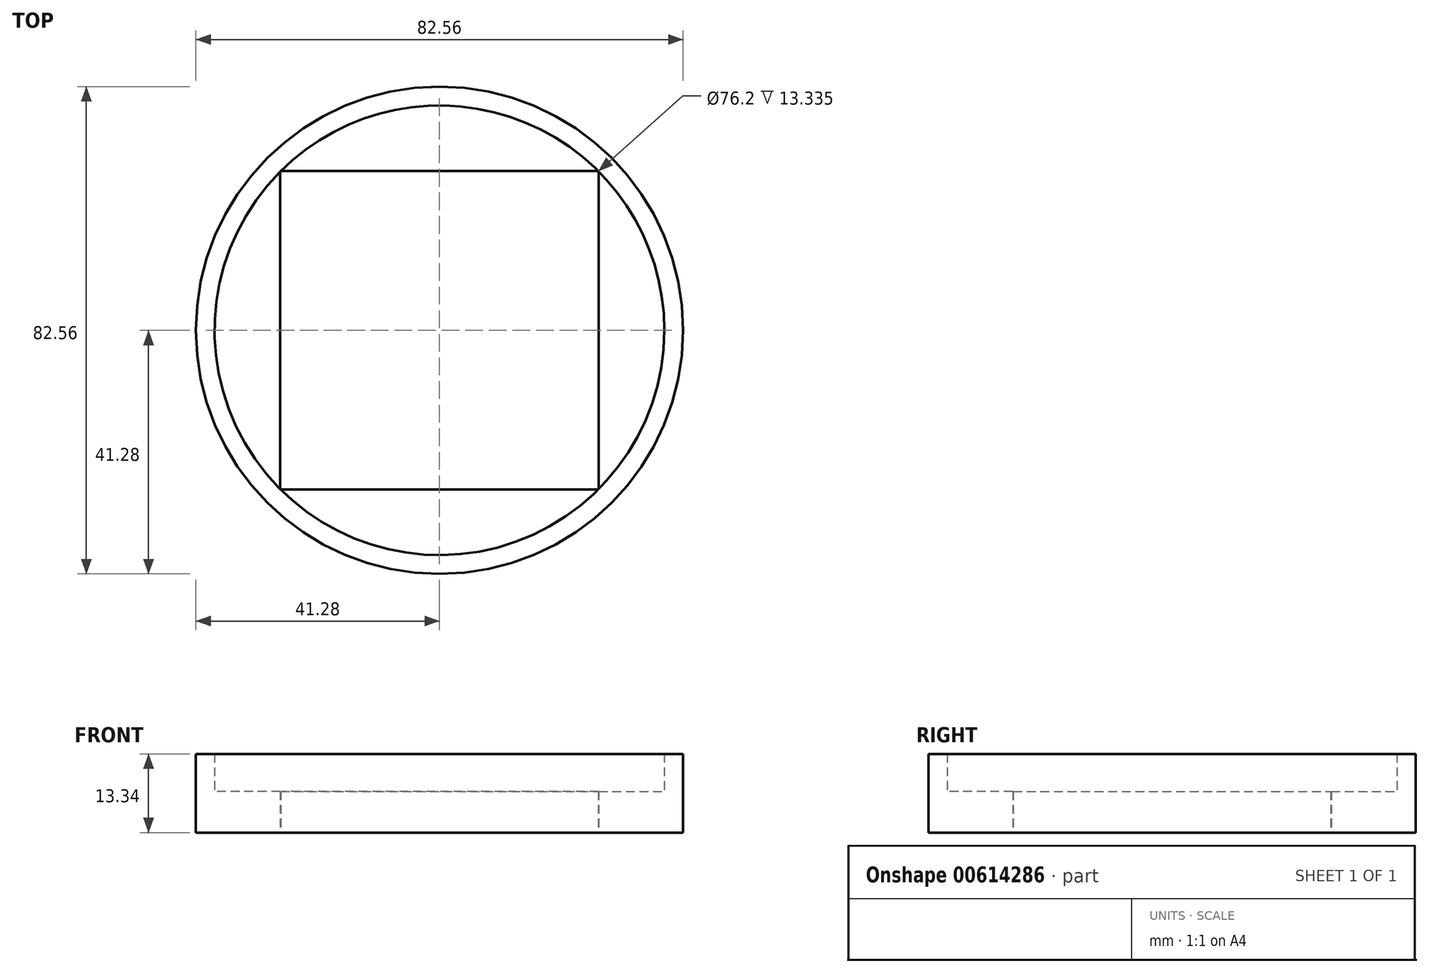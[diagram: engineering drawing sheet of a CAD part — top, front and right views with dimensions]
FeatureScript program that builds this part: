
annotation { "Feature Type Name" : "Feature", "Feature Type Description" : "" }
export const myFeature = defineFeature(function(context is Context, id is Id, definition is map)
    precondition{}
    {
        {
            var Q0;
            Q0=qCreatedBy(makeId("Top.planeOp"),FACE);
            var sketch = newSketch(context, id + "F0", { "sketchPlane" : qUnion([Q0])});
            skCircle(sketch, "E0", {"center": v(0, 0) * mm, "radius": 38.1 * mm});
            skCircle(sketch, "E1", {"center": v(0, 0) * mm, "radius": 41.28 * mm});
            skSolve(sketch);
        }
        {
            var Q0;
            Q0=makeQuery(id+"F0.imprint","IMPRINT",FACE,{"disambiguationData":[TD([[makeQuery(id+"F0.imprint","IMPRINT",EDGE,{"derivedFrom":sQuery(id+"F0.wireOp",EDGE,"E0")}),1.0]])]});
            var sketch = newSketch(context, id + "F1", { "sketchPlane" : qUnion([Q0])});
            skLineSegment(sketch, "E2.bottom", {"start": v(28.58, 28.58) * mm, "end": v(-28.57, 28.58) * mm});
            skLineSegment(sketch, "E2.top", {"start": v(28.58, -28.58) * mm, "end": v(-28.58, -28.58) * mm});
            skLineSegment(sketch, "E2.left", {"start": v(28.58, 28.58) * mm, "end": v(28.58, -28.58) * mm});
            skLineSegment(sketch, "E2.right", {"start": v(-28.57, 28.58) * mm, "end": v(-28.58, -28.58) * mm});
            skPoint(sketch, "E2.middle", {"position": v(0, 0) * mm});
            skLineSegment(sketch, "E3.bottom", {"start": v(26.99, -26.99) * mm, "end": v(-26.99, -26.99) * mm});
            skLineSegment(sketch, "E3.top", {"start": v(26.99, 26.99) * mm, "end": v(-26.99, 26.99) * mm});
            skLineSegment(sketch, "E3.left", {"start": v(26.99, -26.99) * mm, "end": v(26.99, 26.99) * mm});
            skLineSegment(sketch, "E3.right", {"start": v(-26.99, -26.99) * mm, "end": v(-26.99, 26.99) * mm});
            skSolve(sketch);
        }
        {
            var Q0;
            Q0=makeQuery(id+"F0.imprint","IMPRINT",FACE,{"disambiguationData":[TD([[makeQuery(id+"F0.imprint","IMPRINT",EDGE,{"derivedFrom":sQuery(id+"F0.wireOp",EDGE,"E0")}),-1.0]])]});
            extrude(context, id + "F2", {"entities" : qUnion([Q0]), "depth" : 13.33 * mm, "offsetDistance" : 25.4 * mm});
        }
        {
            var Q0;
            {var subQ0=sQuery(id+"F1.wireOp",EDGE,"E2.right");var subQ1=makeQuery(id+"F0.imprint","IMPRINT",EDGE,{"derivedFrom":sQuery(id+"F0.wireOp",EDGE,"E0")});var subQ2=makeQuery(id+"F1.imprint","INTERSECT",VERTEX,{"disambiguationData":[OD(0.0)],"derivedFrom":[subQ1,subQ0]});Q0=makeQuery(id+"F1.imprint","IMPRINT",FACE,{"disambiguationData":[TD([[makeQuery(id+"F1.imprint","IMPRINT",EDGE,{"disambiguationData":[TD([[subQ2,-1.0]])],"derivedFrom":subQ0}),1.0]])]});}
            var Q1;
            {var subQ0=sQuery(id+"F1.wireOp",EDGE,"E2.bottom");var subQ1=makeQuery(id+"F0.imprint","IMPRINT",EDGE,{"derivedFrom":sQuery(id+"F0.wireOp",EDGE,"E0")});var subQ2=makeQuery(id+"F1.imprint","INTERSECT",VERTEX,{"disambiguationData":[OD(0.0)],"derivedFrom":[subQ1,subQ0]});Q1=makeQuery(id+"F1.imprint","IMPRINT",FACE,{"disambiguationData":[TD([[makeQuery(id+"F1.imprint","IMPRINT",EDGE,{"disambiguationData":[TD([[subQ2,-1.0]])],"derivedFrom":subQ0}),1.0]])]});}
            var Q2;
            {var subQ0=sQuery(id+"F1.wireOp",EDGE,"E2.left");var subQ1=makeQuery(id+"F0.imprint","IMPRINT",EDGE,{"derivedFrom":sQuery(id+"F0.wireOp",EDGE,"E0")});var subQ2=makeQuery(id+"F1.imprint","INTERSECT",VERTEX,{"disambiguationData":[OD(0.0)],"derivedFrom":[subQ1,subQ0]});Q2=makeQuery(id+"F1.imprint","IMPRINT",FACE,{"disambiguationData":[TD([[makeQuery(id+"F1.imprint","IMPRINT",EDGE,{"disambiguationData":[TD([[subQ2,-1.0]])],"derivedFrom":subQ0}),-1.0]])]});}
            var Q3;
            {var subQ0=sQuery(id+"F1.wireOp",EDGE,"E2.top");var subQ1=makeQuery(id+"F0.imprint","IMPRINT",EDGE,{"derivedFrom":sQuery(id+"F0.wireOp",EDGE,"E0")});var subQ2=makeQuery(id+"F1.imprint","INTERSECT",VERTEX,{"disambiguationData":[OD(0.0)],"derivedFrom":[subQ1,subQ0]});Q3=makeQuery(id+"F1.imprint","IMPRINT",FACE,{"disambiguationData":[TD([[makeQuery(id+"F1.imprint","IMPRINT",EDGE,{"disambiguationData":[TD([[subQ2,-1.0]])],"derivedFrom":subQ0}),-1.0]])]});}
            var Q4;
            {var subQ0=sQuery(id+"F1.wireOp",EDGE,"E2.bottom");var subQ1=makeQuery(id+"F0.imprint","IMPRINT",EDGE,{"derivedFrom":sQuery(id+"F0.wireOp",EDGE,"E0")});var subQ2=makeQuery(id+"F1.imprint","INTERSECT",VERTEX,{"disambiguationData":[OD(0.0)],"derivedFrom":[subQ1,subQ0]});Q4=makeQuery(id+"F1.imprint","IMPRINT",FACE,{"disambiguationData":[TD([[makeQuery(id+"F1.imprint","IMPRINT",EDGE,{"disambiguationData":[TD([[subQ2,-1.0]])],"derivedFrom":subQ0}),-1.0]])]});}
            var Q5;
            {var subQ0=sQuery(id+"F1.wireOp",EDGE,"E2.right");var subQ1=makeQuery(id+"F0.imprint","IMPRINT",EDGE,{"derivedFrom":sQuery(id+"F0.wireOp",EDGE,"E0")});var subQ2=makeQuery(id+"F1.imprint","INTERSECT",VERTEX,{"disambiguationData":[OD(0.0)],"derivedFrom":[subQ1,subQ0]});Q5=makeQuery(id+"F1.imprint","IMPRINT",FACE,{"disambiguationData":[TD([[makeQuery(id+"F1.imprint","IMPRINT",EDGE,{"disambiguationData":[TD([[subQ2,-1.0]])],"derivedFrom":subQ0}),-1.0]])]});}
            var Q6;
            {var subQ0=sQuery(id+"F1.wireOp",EDGE,"E2.top");var subQ1=makeQuery(id+"F0.imprint","IMPRINT",EDGE,{"derivedFrom":sQuery(id+"F0.wireOp",EDGE,"E0")});var subQ2=makeQuery(id+"F1.imprint","INTERSECT",VERTEX,{"disambiguationData":[OD(0.0)],"derivedFrom":[subQ1,subQ0]});Q6=makeQuery(id+"F1.imprint","IMPRINT",FACE,{"disambiguationData":[TD([[makeQuery(id+"F1.imprint","IMPRINT",EDGE,{"disambiguationData":[TD([[subQ2,-1.0]])],"derivedFrom":subQ0}),1.0]])]});}
            var Q7;
            {var subQ0=sQuery(id+"F1.wireOp",EDGE,"E2.left");var subQ1=makeQuery(id+"F0.imprint","IMPRINT",EDGE,{"derivedFrom":sQuery(id+"F0.wireOp",EDGE,"E0")});var subQ2=makeQuery(id+"F1.imprint","INTERSECT",VERTEX,{"disambiguationData":[OD(0.0)],"derivedFrom":[subQ1,subQ0]});Q7=makeQuery(id+"F1.imprint","IMPRINT",FACE,{"disambiguationData":[TD([[makeQuery(id+"F1.imprint","IMPRINT",EDGE,{"disambiguationData":[TD([[subQ2,-1.0]])],"derivedFrom":subQ0}),1.0]])]});}
            extrude(context, id + "F3", {"entities" : qUnion([Q0, Q1, Q2, Q3, Q4, Q5, Q6, Q7]), "operationType" : NewBodyOperationType.ADD, "depth" : 7 * mm, "offsetDistance" : 25.4 * mm});
        }
    });
